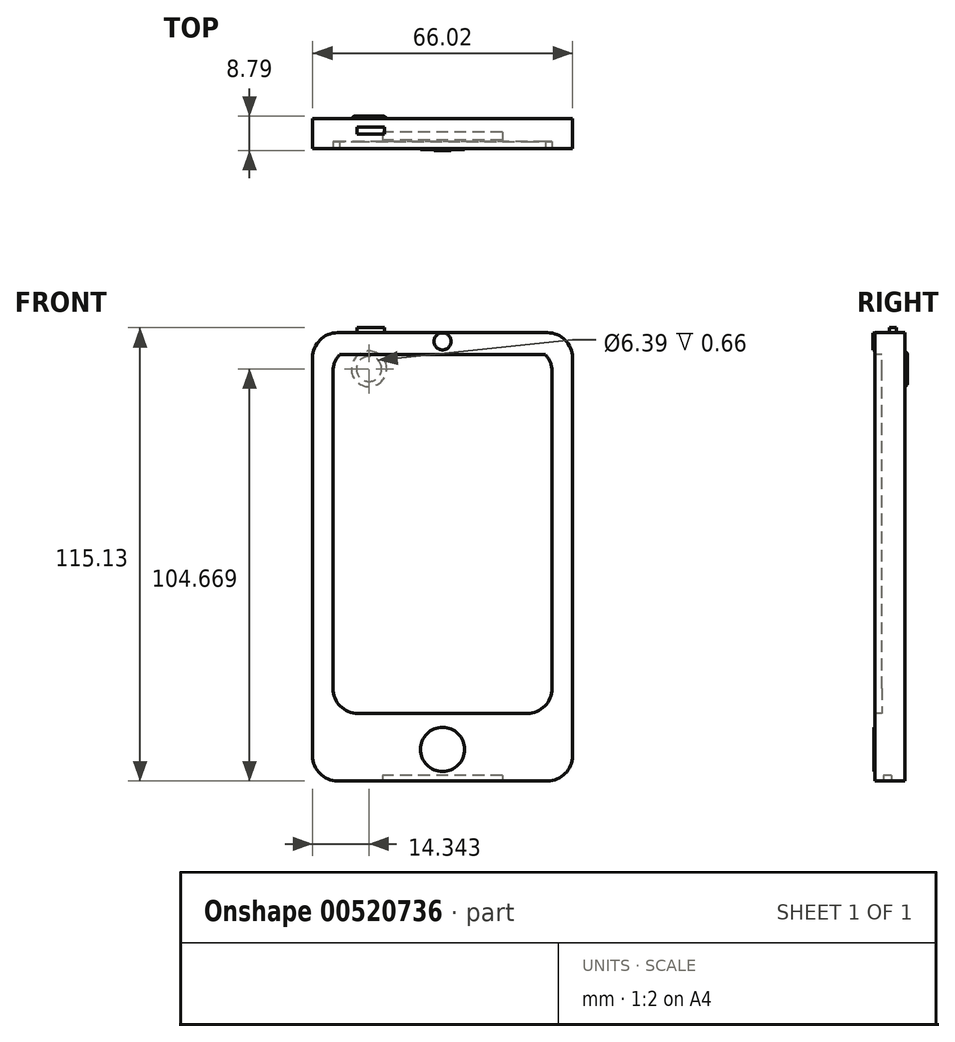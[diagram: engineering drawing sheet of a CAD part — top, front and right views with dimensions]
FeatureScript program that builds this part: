
annotation { "Feature Type Name" : "Feature", "Feature Type Description" : "" }
export const myFeature = defineFeature(function(context is Context, id is Id, definition is map)
    precondition{}
    {
        {
            var Q0;
            Q0=qCreatedBy(makeId("Front.planeOp"),FACE);
            var sketch = newSketch(context, id + "F0", { "sketchPlane" : qUnion([Q0])});
            skLineSegment(sketch, "E0.bottom", {"start": v(26.66, 56.93) * mm, "end": v(-26.66, 56.93) * mm});
            skLineSegment(sketch, "E0.top", {"start": v(26.66, -56.93) * mm, "end": v(-26.66, -56.93) * mm});
            skLineSegment(sketch, "E0.left", {"start": v(33, 50.58) * mm, "end": v(33, -50.58) * mm});
            skLineSegment(sketch, "E0.right", {"start": v(-33, 50.58) * mm, "end": v(-33, -50.58) * mm});
            skPoint(sketch, "E0.middle", {"position": v(0, 0) * mm});
            skPoint(sketch, "E1.visualSharp", {"position": v(-33, 56.93) * mm});
            skArc(sketch, "E1.filletArc", {"start": v(-26.66, 56.93) * mm, "mid": v(-31.15, 55.07) * mm, "end": v(-33, 50.58) * mm});
            skPoint(sketch, "E2.visualSharp", {"position": v(33, 56.93) * mm});
            skArc(sketch, "E2.filletArc", {"start": v(33, 50.58) * mm, "mid": v(31.15, 55.07) * mm, "end": v(26.66, 56.93) * mm});
            skPoint(sketch, "E3.visualSharp", {"position": v(33, -56.93) * mm});
            skArc(sketch, "E3.filletArc", {"start": v(26.66, -56.93) * mm, "mid": v(31.15, -55.07) * mm, "end": v(33, -50.58) * mm});
            skPoint(sketch, "E4.visualSharp", {"position": v(-33, -56.93) * mm});
            skArc(sketch, "E4.filletArc", {"start": v(-33, -50.58) * mm, "mid": v(-31.15, -55.07) * mm, "end": v(-26.66, -56.93) * mm});
            skSolve(sketch);
        }
        {
            var Q0;
            Q0=makeQuery(id+"F0.imprint","IMPRINT",FACE,{"disambiguationData":[TD([[makeQuery(id+"F0.imprint","IMPRINT",EDGE,{"derivedFrom":sQuery(id+"F0.wireOp",EDGE,"E0.bottom")}),1.0]])]});
            extrude(context, id + "F1", {"entities" : qUnion([Q0]), "depth" : 7.62 * mm, "offsetDistance" : 25.4 * mm});
        }
        {
            var Q0;
            Q0=makeQuery(id+"F1.opExtrude","CAP_FACE",FACE,{"disambiguationData":[OSD([sQuery(id+"F0.wireOp",EDGE,"E0.bottom"),sQuery(id+"F0.wireOp",EDGE,"E0.top"),sQuery(id+"F0.wireOp",EDGE,"E0.left"),sQuery(id+"F0.wireOp",EDGE,"E0.right"),sQuery(id+"F0.wireOp",EDGE,"E1.filletArc"),sQuery(id+"F0.wireOp",EDGE,"E2.filletArc"),sQuery(id+"F0.wireOp",EDGE,"E3.filletArc"),sQuery(id+"F0.wireOp",EDGE,"E4.filletArc")])],"isStart":false});
            var sketch = newSketch(context, id + "F2", { "sketchPlane" : qUnion([Q0])});
            skLineSegment(sketch, "E5.top", {"start": v(21.5, 53.33) * mm, "end": v(-21.5, 53.33) * mm});
            skLineSegment(sketch, "E5.left", {"start": v(27.86, -33.42) * mm, "end": v(27.86, 46.98) * mm});
            skLineSegment(sketch, "E5.right", {"start": v(-27.86, -33.42) * mm, "end": v(-27.86, 46.98) * mm});
            skPoint(sketch, "E5.middle", {"position": v(0, 0) * mm});
            skLineSegment(sketch, "E6", {"start": v(-21.5, -39.77) * mm, "end": v(21.5, -39.77) * mm});
            skPoint(sketch, "E5.bottom.end.orphan", {"position": v(-27.86, -53.33) * mm});
            skPoint(sketch, "E7.orphan", {"position": v(27.86, -53.33) * mm});
            skPoint(sketch, "E8.visualSharp", {"position": v(-27.86, 53.33) * mm});
            skArc(sketch, "E8.filletArc", {"start": v(-21.5, 53.33) * mm, "mid": v(-26, 51.47) * mm, "end": v(-27.86, 46.98) * mm});
            skPoint(sketch, "E9.visualSharp", {"position": v(27.86, 53.33) * mm});
            skArc(sketch, "E9.filletArc", {"start": v(27.86, 46.98) * mm, "mid": v(26, 51.47) * mm, "end": v(21.5, 53.33) * mm});
            skPoint(sketch, "E10.visualSharp", {"position": v(27.86, -39.77) * mm});
            skArc(sketch, "E10.filletArc", {"start": v(21.5, -39.77) * mm, "mid": v(26, -37.91) * mm, "end": v(27.86, -33.42) * mm});
            skPoint(sketch, "E11.visualSharp", {"position": v(-27.86, -39.77) * mm});
            skArc(sketch, "E11.filletArc", {"start": v(-27.86, -33.42) * mm, "mid": v(-26, -37.91) * mm, "end": v(-21.5, -39.77) * mm});
            skSolve(sketch);
        }
        {
            var Q0;
            Q0=makeQuery(id+"F2.imprint","IMPRINT",FACE,{"disambiguationData":[TD([[makeQuery(id+"F2.imprint","IMPRINT",EDGE,{"derivedFrom":sQuery(id+"F2.wireOp",EDGE,"E5.top")}),1.0]])]});
            extrude(context, id + "F3", {"entities" : qUnion([Q0]), "operationType" : NewBodyOperationType.REMOVE, "oppositeDirection" : true, "depth" : 1.78 * mm, "offsetDistance" : 25.4 * mm});
        }
        {
            var Q0;
            Q0=makeQuery(id+"F1.opExtrude","CAP_FACE",FACE,{"disambiguationData":[OSD([sQuery(id+"F0.wireOp",EDGE,"E0.bottom"),sQuery(id+"F0.wireOp",EDGE,"E0.top"),sQuery(id+"F0.wireOp",EDGE,"E0.left"),sQuery(id+"F0.wireOp",EDGE,"E0.right"),sQuery(id+"F0.wireOp",EDGE,"E1.filletArc"),sQuery(id+"F0.wireOp",EDGE,"E2.filletArc"),sQuery(id+"F0.wireOp",EDGE,"E3.filletArc"),sQuery(id+"F0.wireOp",EDGE,"E4.filletArc")])],"isStart":false});
            var sketch = newSketch(context, id + "F4", { "sketchPlane" : qUnion([Q0])});
            skCircle(sketch, "E12", {"center": v(0, -48.93) * mm, "radius": 5.6 * mm});
            skSolve(sketch);
        }
        {
            var Q0;
            Q0=makeQuery(id+"F1.opExtrude","SWEPT_FACE",FACE,{"disambiguationData":[OSD([sQuery(id+"F0.wireOp",EDGE,"E0.right")])]});
            var sketch = newSketch(context, id + "F5", { "sketchPlane" : qUnion([Q0])});
            skLineSegment(sketch, "E13.bottom", {"start": v(5, 24.2) * mm, "end": v(2.65, 24.2) * mm});
            skLineSegment(sketch, "E13.top", {"start": v(5, 42.45) * mm, "end": v(2.65, 42.45) * mm});
            skLineSegment(sketch, "E13.left", {"start": v(5, 24.2) * mm, "end": v(5, 42.45) * mm});
            skLineSegment(sketch, "E13.right", {"start": v(2.65, 24.2) * mm, "end": v(2.65, 42.45) * mm});
            skPoint(sketch, "E13.middle", {"position": v(3.83, 33.32) * mm});
            skSolve(sketch);
        }
        {
            var Q0;
            Q0=makeQuery(id+"F4.imprint","IMPRINT",FACE,{"disambiguationData":[TD([[makeQuery(id+"F4.imprint","IMPRINT",EDGE,{"derivedFrom":sQuery(id+"F4.wireOp",EDGE,"E12")}),1.0]])]});
            extrude(context, id + "F6", {"entities" : qUnion([Q0]), "operationType" : NewBodyOperationType.ADD, "depth" : 0.25 * mm, "offsetDistance" : 25.4 * mm});
        }
        {
            var Q0;
            Q0=makeQuery(id+"F5.imprint","IMPRINT",FACE,{"disambiguationData":[TD([[makeQuery(id+"F5.imprint","IMPRINT",EDGE,{"derivedFrom":sQuery(id+"F5.wireOp",EDGE,"E13.bottom")}),1.0]])]});
            var sketch = newSketch(context, id + "F7", { "sketchPlane" : qUnion([Q0])});
            skCircle(sketch, "E14", {"center": v(4.04, 11.81) * mm, "radius": 2.27 * mm});
            skCircle(sketch, "E15", {"center": v(3.77, 4.15) * mm, "radius": 2.27 * mm});
            skSolve(sketch);
        }
        {
            var Q0;
            Q0=sQuery(id+"F7.wireOp",EDGE,"E15");
            var Q1;
            Q1=sQuery(id+"F7.wireOp",EDGE,"E14");
            var Q2;
            Q2=sQuery(id+"F5.wireOp",EDGE,"E13.right");
            var Q3;
            Q3=sQuery(id+"F5.wireOp",EDGE,"E13.bottom");
            var Q4;
            Q4=sQuery(id+"F5.wireOp",EDGE,"E13.top");
            var Q5;
            Q5=sQuery(id+"F5.wireOp",EDGE,"E13.left");
            extrude(context, id + "F8", {"bodyType" : ToolBodyType.SURFACE, "surfaceEntities" : qUnion([Q0, Q1, Q2, Q3, Q4, Q5]), "depth" : 0.25 * mm, "offsetDistance" : 25.4 * mm});
        }
        {
            var Q0;
            Q0=makeQuery(id+"F1.opExtrude","SWEPT_FACE",FACE,{"disambiguationData":[OSD([sQuery(id+"F0.wireOp",EDGE,"E0.top")])]});
            var sketch = newSketch(context, id + "F9", { "sketchPlane" : qUnion([Q0])});
            skCircle(sketch, "E16", {"center": v(-22.77, 3.81) * mm, "radius": 2.53 * mm});
            skPoint(sketch, "E16.centerSnap0", {"position": v(-26.66, 3.81) * mm});
            skSolve(sketch);
        }
        {
            var Q0;
            Q0=sQuery(id+"F9.wireOp",EDGE,"E16");
            extrude(context, id + "F10", {"bodyType" : ToolBodyType.SURFACE, "surfaceEntities" : qUnion([Q0]), "oppositeDirection" : true, "depth" : 11.68 * mm, "offsetDistance" : 25.4 * mm});
        }
        {
            var Q0;
            Q0=makeQuery(id+"F1.opExtrude","SWEPT_FACE",FACE,{"disambiguationData":[OSD([sQuery(id+"F0.wireOp",EDGE,"E0.bottom")])]});
            var sketch = newSketch(context, id + "F11", { "sketchPlane" : qUnion([Q0])});
            skPoint(sketch, "E17.oppositeSnap0", {"position": v(26.66, -3.81) * mm});
            skLineSegment(sketch, "E17.bottom", {"start": v(17.9, -2.92) * mm, "end": v(23.74, -2.92) * mm});
            skLineSegment(sketch, "E17.top", {"start": v(17.9, -3.81) * mm, "end": v(23.74, -3.81) * mm});
            skLineSegment(sketch, "E17.left", {"start": v(17.9, -2.92) * mm, "end": v(17.9, -3.81) * mm});
            skLineSegment(sketch, "E17.right", {"start": v(23.74, -2.92) * mm, "end": v(23.74, -3.81) * mm});
            skSolve(sketch);
        }
        {
            var Q0;
            Q0=makeQuery(id+"F11.imprint","IMPRINT",FACE,{"disambiguationData":[TD([[makeQuery(id+"F11.imprint","IMPRINT",EDGE,{"derivedFrom":sQuery(id+"F11.wireOp",EDGE,"E17.bottom")}),-1.0]])]});
            extrude(context, id + "F12", {"entities" : qUnion([Q0]), "operationType" : NewBodyOperationType.ADD, "oppositeDirection" : true, "depth" : 0.25 * mm, "offsetDistance" : 25.4 * mm});
        }
        {
            var Q0;
            Q0=makeQuery(id+"F1.opExtrude","SWEPT_FACE",FACE,{"disambiguationData":[OSD([sQuery(id+"F0.wireOp",EDGE,"E0.bottom")])]});
            var sketch = newSketch(context, id + "F13", { "sketchPlane" : qUnion([Q0])});
            skPoint(sketch, "E18.oppositeSnap0", {"position": v(26.66, -3.81) * mm});
            skLineSegment(sketch, "E18.bottom", {"start": v(19.66, -4.67) * mm, "end": v(23.45, -4.67) * mm});
            skLineSegment(sketch, "E18.top", {"start": v(19.66, -3.81) * mm, "end": v(23.45, -3.81) * mm});
            skLineSegment(sketch, "E18.left", {"start": v(19.66, -4.67) * mm, "end": v(19.66, -3.81) * mm});
            skLineSegment(sketch, "E18.right", {"start": v(23.45, -4.67) * mm, "end": v(23.45, -3.81) * mm});
            skSolve(sketch);
        }
        {
            var Q0;
            Q0=makeQuery(id+"F13.imprint","IMPRINT",FACE,{"disambiguationData":[TD([[makeQuery(id+"F13.imprint","IMPRINT",EDGE,{"derivedFrom":sQuery(id+"F13.wireOp",EDGE,"E18.bottom")}),-1.0]])]});
            extrude(context, id + "F14", {"entities" : qUnion([Q0]), "operationType" : NewBodyOperationType.ADD, "oppositeDirection" : true, "depth" : 5.6 * mm, "offsetDistance" : 25.4 * mm});
        }
        {
            var Q0;
            Q0=makeQuery(id+"F1.opExtrude","SWEPT_FACE",FACE,{"disambiguationData":[OSD([sQuery(id+"F0.wireOp",EDGE,"E0.bottom")])]});
            var sketch = newSketch(context, id + "F15", { "sketchPlane" : qUnion([Q0])});
            skLineSegment(sketch, "E19.bottom", {"start": v(21.45, -4.06) * mm, "end": v(16, -4.06) * mm});
            skLineSegment(sketch, "E19.top", {"start": v(21.45, -2.59) * mm, "end": v(16, -2.59) * mm});
            skLineSegment(sketch, "E19.left", {"start": v(21.45, -4.06) * mm, "end": v(21.45, -2.59) * mm});
            skLineSegment(sketch, "E19.right", {"start": v(16, -4.06) * mm, "end": v(16, -2.59) * mm});
            skLineSegment(sketch, "E20.bottom", {"start": v(16, -2.59) * mm, "end": v(16, -2.59) * mm});
            skLineSegment(sketch, "E20.top", {"start": v(16, -4.06) * mm, "end": v(16, -4.06) * mm});
            skLineSegment(sketch, "E20.left", {"start": v(16, -2.59) * mm, "end": v(16, -4.06) * mm});
            skLineSegment(sketch, "E20.right", {"start": v(16, -2.59) * mm, "end": v(16, -4.06) * mm});
            skSolve(sketch);
        }
        {
            var Q0;
            Q0=makeQuery(id+"F15.imprint","IMPRINT",FACE,{"disambiguationData":[TD([[makeQuery(id+"F15.imprint","IMPRINT",EDGE,{"derivedFrom":sQuery(id+"F15.wireOp",EDGE,"E19.bottom")}),-1.0]])]});
            extrude(context, id + "F16", {"entities" : qUnion([Q0]), "operationType" : NewBodyOperationType.ADD, "oppositeDirection" : true, "depth" : 2.92 * mm, "offsetDistance" : 25.4 * mm});
        }
        {
            var Q0;
            Q0=makeQuery(id+"F1.opExtrude","SWEPT_FACE",FACE,{"disambiguationData":[OSD([sQuery(id+"F0.wireOp",EDGE,"E0.bottom")])]});
            var sketch = newSketch(context, id + "F17", { "sketchPlane" : qUnion([Q0])});
            skLineSegment(sketch, "E21.bottom", {"start": v(-21.69, -3.95) * mm, "end": v(-14.68, -3.95) * mm});
            skLineSegment(sketch, "E21.top", {"start": v(-21.69, -2.14) * mm, "end": v(-14.68, -2.14) * mm});
            skLineSegment(sketch, "E21.left", {"start": v(-21.69, -3.95) * mm, "end": v(-21.69, -2.14) * mm});
            skLineSegment(sketch, "E21.right", {"start": v(-14.68, -3.95) * mm, "end": v(-14.68, -2.14) * mm});
            skSolve(sketch);
        }
        {
            var Q0;
            Q0=makeQuery(id+"F17.imprint","IMPRINT",FACE,{"disambiguationData":[TD([[makeQuery(id+"F17.imprint","IMPRINT",EDGE,{"derivedFrom":sQuery(id+"F17.wireOp",EDGE,"E21.bottom")}),1.0]])]});
            extrude(context, id + "F18", {"entities" : qUnion([Q0]), "operationType" : NewBodyOperationType.ADD, "depth" : 1.27 * mm, "offsetDistance" : 25.4 * mm});
        }
        {
            var Q0;
            {var subQ0=sQuery(id+"F0.wireOp",EDGE,"E0.bottom");Q0=makeQuery(id+"F14.boolean.opBoolean","MERGE",FACE,{"derivedFrom":[makeQuery(id+"F1.opExtrude","CAP_FACE",FACE,{"disambiguationData":[OSD([subQ0,sQuery(id+"F0.wireOp",EDGE,"E0.top"),sQuery(id+"F0.wireOp",EDGE,"E0.left"),sQuery(id+"F0.wireOp",EDGE,"E0.right"),sQuery(id+"F0.wireOp",EDGE,"E1.filletArc"),sQuery(id+"F0.wireOp",EDGE,"E2.filletArc"),sQuery(id+"F0.wireOp",EDGE,"E3.filletArc"),sQuery(id+"F0.wireOp",EDGE,"E4.filletArc")])],"isStart":false}),makeQuery(id+"F14.opExtrude","SWEPT_FACE",FACE,{"disambiguationData":[OSD([subQ0]),TDD([makeQuery(id+"F13.imprint","IMPRINT",EDGE,{"derivedFrom":makeQuery(id+"F1.opExtrude","CAP_EDGE",EDGE,{"disambiguationData":[OSD([subQ0])],"isStart":false})})])]})]});}
            var sketch = newSketch(context, id + "F19", { "sketchPlane" : qUnion([Q0])});
            skCircle(sketch, "E22", {"center": v(0, 54.75) * mm, "radius": 2.16 * mm});
            skSolve(sketch);
        }
        {
            var Q0;
            Q0=makeQuery(id+"F19.imprint","IMPRINT",FACE,{"disambiguationData":[TD([[makeQuery(id+"F19.imprint","IMPRINT",EDGE,{"derivedFrom":sQuery(id+"F19.wireOp",EDGE,"E22")}),1.0]])]});
            extrude(context, id + "F20", {"entities" : qUnion([Q0]), "operationType" : NewBodyOperationType.ADD, "depth" : 0.5 * mm, "offsetDistance" : 25.4 * mm});
        }
        {
            var Q0;
            Q0=makeQuery(id+"F1.opExtrude","CAP_FACE",FACE,{"disambiguationData":[OSD([sQuery(id+"F0.wireOp",EDGE,"E0.bottom"),sQuery(id+"F0.wireOp",EDGE,"E0.top"),sQuery(id+"F0.wireOp",EDGE,"E0.left"),sQuery(id+"F0.wireOp",EDGE,"E0.right"),sQuery(id+"F0.wireOp",EDGE,"E1.filletArc"),sQuery(id+"F0.wireOp",EDGE,"E2.filletArc"),sQuery(id+"F0.wireOp",EDGE,"E3.filletArc"),sQuery(id+"F0.wireOp",EDGE,"E4.filletArc")])],"isStart":true});
            var sketch = newSketch(context, id + "F21", { "sketchPlane" : qUnion([Q0])});
            skCircle(sketch, "E23", {"center": v(24.06, 50.7) * mm, "radius": 3.83 * mm});
            skSolve(sketch);
        }
        {
            var Q0;
            Q0=makeQuery(id+"F21.imprint","IMPRINT",FACE,{"disambiguationData":[TD([[makeQuery(id+"F21.imprint","IMPRINT",EDGE,{"derivedFrom":sQuery(id+"F21.wireOp",EDGE,"E23")}),1.0]])]});
            extrude(context, id + "F22", {"entities" : qUnion([Q0]), "operationType" : NewBodyOperationType.ADD, "oppositeDirection" : true, "depth" : 2.3 * mm, "offsetDistance" : 25.4 * mm});
        }
        {
            var Q0;
            Q0=makeQuery(id+"F1.opExtrude","CAP_FACE",FACE,{"disambiguationData":[OSD([sQuery(id+"F0.wireOp",EDGE,"E0.bottom"),sQuery(id+"F0.wireOp",EDGE,"E0.top"),sQuery(id+"F0.wireOp",EDGE,"E0.left"),sQuery(id+"F0.wireOp",EDGE,"E0.right"),sQuery(id+"F0.wireOp",EDGE,"E1.filletArc"),sQuery(id+"F0.wireOp",EDGE,"E2.filletArc"),sQuery(id+"F0.wireOp",EDGE,"E3.filletArc"),sQuery(id+"F0.wireOp",EDGE,"E4.filletArc")])],"isStart":true});
            var sketch = newSketch(context, id + "F23", { "sketchPlane" : qUnion([Q0])});
            skCircle(sketch, "E24", {"center": v(18.67, 47.74) * mm, "radius": 4.5 * mm});
            skCircle(sketch, "E25", {"center": v(18.67, 47.74) * mm, "radius": 3.2 * mm});
            skSolve(sketch);
        }
        {
            var Q0;
            Q0=makeQuery(id+"F23.imprint","IMPRINT",FACE,{"disambiguationData":[TD([[makeQuery(id+"F23.imprint","IMPRINT",EDGE,{"derivedFrom":sQuery(id+"F23.wireOp",EDGE,"E24")}),1.0]])]});
            extrude(context, id + "F24", {"entities" : qUnion([Q0]), "depth" : 0.66 * mm, "offsetDistance" : 25.4 * mm});
        }
        {
            var Q0;
            Q0=makeQuery(id+"F24.opExtrude","CAP_EDGE",EDGE,{"disambiguationData":[OSD([sQuery(id+"F23.wireOp",EDGE,"E24")])],"isStart":false});
            fillet(context, id + "F25", {"entities" : qUnion([Q0]), "radius" : 1.27 * mm, "tangentPropagation" : true, "allowEdgeOverflow" : false});
        }
        {
            var Q0;
            Q0=makeQuery(id+"F1.opExtrude","SWEPT_FACE",FACE,{"disambiguationData":[OSD([sQuery(id+"F0.wireOp",EDGE,"E0.top")])]});
            var sketch = newSketch(context, id + "F26", { "sketchPlane" : qUnion([Q0])});
            skLineSegment(sketch, "E26.bottom", {"start": v(-3.41, 5.26) * mm, "end": v(5.64, 5.26) * mm});
            skLineSegment(sketch, "E26.top", {"start": v(-3.41, 3.5) * mm, "end": v(5.64, 3.5) * mm});
            skLineSegment(sketch, "E26.left", {"start": v(-3.41, 5.26) * mm, "end": v(-3.41, 3.5) * mm});
            skLineSegment(sketch, "E26.right", {"start": v(5.64, 5.26) * mm, "end": v(5.64, 3.5) * mm});
            skSolve(sketch);
        }
        {
            var Q0;
            Q0=makeQuery(id+"F26.imprint","IMPRINT",FACE,{"disambiguationData":[TD([[makeQuery(id+"F26.imprint","IMPRINT",EDGE,{"derivedFrom":sQuery(id+"F26.wireOp",EDGE,"E26.bottom")}),-1.0]])]});
            extrude(context, id + "F27", {"entities" : qUnion([Q0]), "operationType" : NewBodyOperationType.ADD, "oppositeDirection" : true, "depth" : 12.2 * mm, "offsetDistance" : 25.4 * mm});
        }
        {
            var Q0;
            Q0=makeQuery(id+"F1.opExtrude","SWEPT_FACE",FACE,{"disambiguationData":[OSD([sQuery(id+"F0.wireOp",EDGE,"E0.top")])]});
            var Q1;
            Q1 = qSketchRegion(id + "F26", true);
            extrude(context, id + "F28", {"entities" : qUnion([Q0, Q1]), "operationType" : NewBodyOperationType.ADD, "oppositeDirection" : true, "depth" : 1.27 * mm, "offsetDistance" : 25.4 * mm});
        }
        {
            var Q0;
            Q0=makeQuery(id+"F1.opExtrude","SWEPT_FACE",FACE,{"disambiguationData":[OSD([sQuery(id+"F0.wireOp",EDGE,"E0.top")])]});
            var sketch = newSketch(context, id + "F29", { "sketchPlane" : qUnion([Q0])});
            skLineSegment(sketch, "E27.bottom", {"start": v(-7.5, 3.8) * mm, "end": v(9.73, 3.8) * mm});
            skLineSegment(sketch, "E27.top", {"start": v(-7.5, 5.26) * mm, "end": v(9.73, 5.26) * mm});
            skLineSegment(sketch, "E27.left", {"start": v(-7.5, 3.8) * mm, "end": v(-7.5, 5.26) * mm});
            skLineSegment(sketch, "E27.right", {"start": v(9.73, 3.8) * mm, "end": v(9.73, 5.26) * mm});
            skSolve(sketch);
        }
        {
            var Q0;
            Q0=makeQuery(id+"F29.imprint","IMPRINT",FACE,{"disambiguationData":[TD([[makeQuery(id+"F29.imprint","IMPRINT",EDGE,{"derivedFrom":sQuery(id+"F29.wireOp",EDGE,"E27.bottom")}),1.0]])]});
            extrude(context, id + "F30", {"entities" : qUnion([Q0]), "operationType" : NewBodyOperationType.ADD, "oppositeDirection" : true, "depth" : 3.05 * mm, "offsetDistance" : 25.4 * mm});
        }
        {
            var Q0;
            Q0=makeQuery(id+"F1.opExtrude","SWEPT_FACE",FACE,{"disambiguationData":[OSD([sQuery(id+"F0.wireOp",EDGE,"E0.top")])]});
            var sketch = newSketch(context, id + "F31", { "sketchPlane" : qUnion([Q0])});
            skLineSegment(sketch, "E28.bottom", {"start": v(-3.7, 4.09) * mm, "end": v(8.85, 4.09) * mm});
            skLineSegment(sketch, "E28.top", {"start": v(-3.7, 5.55) * mm, "end": v(8.85, 5.55) * mm});
            skLineSegment(sketch, "E28.left", {"start": v(-3.7, 4.09) * mm, "end": v(-3.7, 5.55) * mm});
            skLineSegment(sketch, "E28.right", {"start": v(8.85, 4.09) * mm, "end": v(8.85, 5.55) * mm});
            skSolve(sketch);
        }
        {
            var Q0;
            Q0=makeQuery(id+"F31.imprint","IMPRINT",FACE,{"disambiguationData":[TD([[makeQuery(id+"F31.imprint","IMPRINT",EDGE,{"derivedFrom":sQuery(id+"F31.wireOp",EDGE,"E28.bottom")}),-1.0]])]});
            extrude(context, id + "F32", {"entities" : qUnion([Q0]), "operationType" : NewBodyOperationType.ADD, "oppositeDirection" : true, "depth" : 1.27 * mm, "offsetDistance" : 25.4 * mm});
        }
        {
            var Q0;
            Q0=makeQuery(id+"F1.opExtrude","SWEPT_FACE",FACE,{"disambiguationData":[OSD([sQuery(id+"F0.wireOp",EDGE,"E0.top")])]});
            var sketch = newSketch(context, id + "F33", { "sketchPlane" : qUnion([Q0])});
            skLineSegment(sketch, "E29.bottom", {"start": v(15.22, 3.47) * mm, "end": v(-15.22, 3.47) * mm});
            skLineSegment(sketch, "E29.top", {"start": v(15.22, 5.51) * mm, "end": v(-15.22, 5.51) * mm});
            skLineSegment(sketch, "E29.left", {"start": v(15.22, 3.47) * mm, "end": v(15.22, 5.51) * mm});
            skLineSegment(sketch, "E29.right", {"start": v(-15.22, 3.47) * mm, "end": v(-15.22, 5.51) * mm});
            skPoint(sketch, "E29.middle", {"position": v(0, 4.5) * mm});
            skSolve(sketch);
        }
        {
            var Q0;
            Q0=makeQuery(id+"F33.imprint","IMPRINT",FACE,{"disambiguationData":[TD([[makeQuery(id+"F33.imprint","IMPRINT",EDGE,{"derivedFrom":sQuery(id+"F33.wireOp",EDGE,"E29.bottom")}),-1.0]])]});
            extrude(context, id + "F34", {"entities" : qUnion([Q0]), "operationType" : NewBodyOperationType.ADD, "depth" : 1.27 * mm, "offsetDistance" : 25.4 * mm});
        }
        {
            var Q0;
            Q0=makeQuery(id+"F34.opExtrude","CAP_FACE",FACE,{"disambiguationData":[OSD([sQuery(id+"F33.wireOp",EDGE,"E29.bottom"),sQuery(id+"F33.wireOp",EDGE,"E29.top"),sQuery(id+"F33.wireOp",EDGE,"E29.left"),sQuery(id+"F33.wireOp",EDGE,"E29.right")])],"isStart":false});
            extrude(context, id + "F35", {"entities" : qUnion([Q0]), "operationType" : NewBodyOperationType.REMOVE, "oppositeDirection" : true, "depth" : 2.67 * mm, "offsetDistance" : 25.4 * mm});
        }
    });
